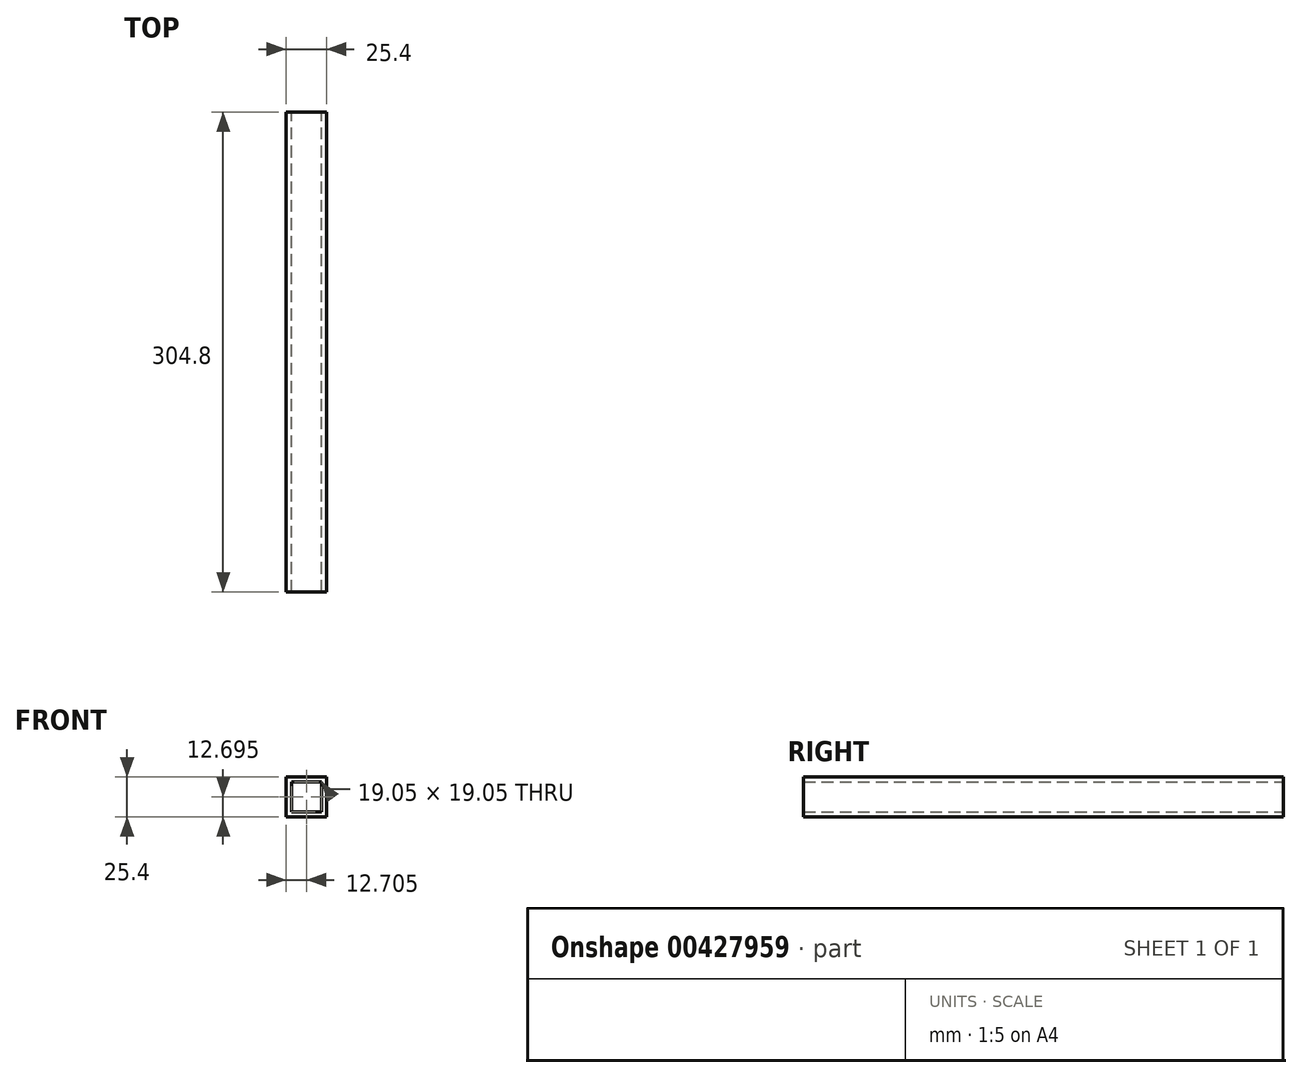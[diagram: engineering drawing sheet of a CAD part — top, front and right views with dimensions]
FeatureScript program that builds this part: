
annotation { "Feature Type Name" : "Feature", "Feature Type Description" : "" }
export const myFeature = defineFeature(function(context is Context, id is Id, definition is map)
    precondition{}
    {
        {
            var Q0;
            Q0=qCreatedBy(makeId("Front.planeOp"),FACE);
            var sketch = newSketch(context, id + "F0", { "sketchPlane" : qUnion([Q0])});
            skLineSegment(sketch, "E0.bottom", {"start": v(-22.23, 22.23) * mm, "end": v(3.17, 22.23) * mm});
            skLineSegment(sketch, "E0.top", {"start": v(-22.23, -3.18) * mm, "end": v(3.18, -3.18) * mm});
            skLineSegment(sketch, "E0.left", {"start": v(-22.23, 22.23) * mm, "end": v(-22.23, -3.18) * mm});
            skLineSegment(sketch, "E0.right", {"start": v(3.17, 22.23) * mm, "end": v(3.18, -3.18) * mm});
            skLineSegment(sketch, "E1.bottom", {"start": v(-19.05, 19.05) * mm, "end": v(0, 19.05) * mm});
            skLineSegment(sketch, "E1.top", {"start": v(-19.05, 0) * mm, "end": v(0, 0) * mm});
            skLineSegment(sketch, "E1.left", {"start": v(-19.05, 19.05) * mm, "end": v(-19.05, 0) * mm});
            skLineSegment(sketch, "E1.right", {"start": v(0, 19.05) * mm, "end": v(0, 0) * mm});
            skSolve(sketch);
        }
        {
            var Q0;
            Q0=qSketchRegion(id+"F0",true);
            extrude(context, id + "F1", {"entities" : qUnion([Q0]), "depth" : 304.8 * mm});
        }
    });
